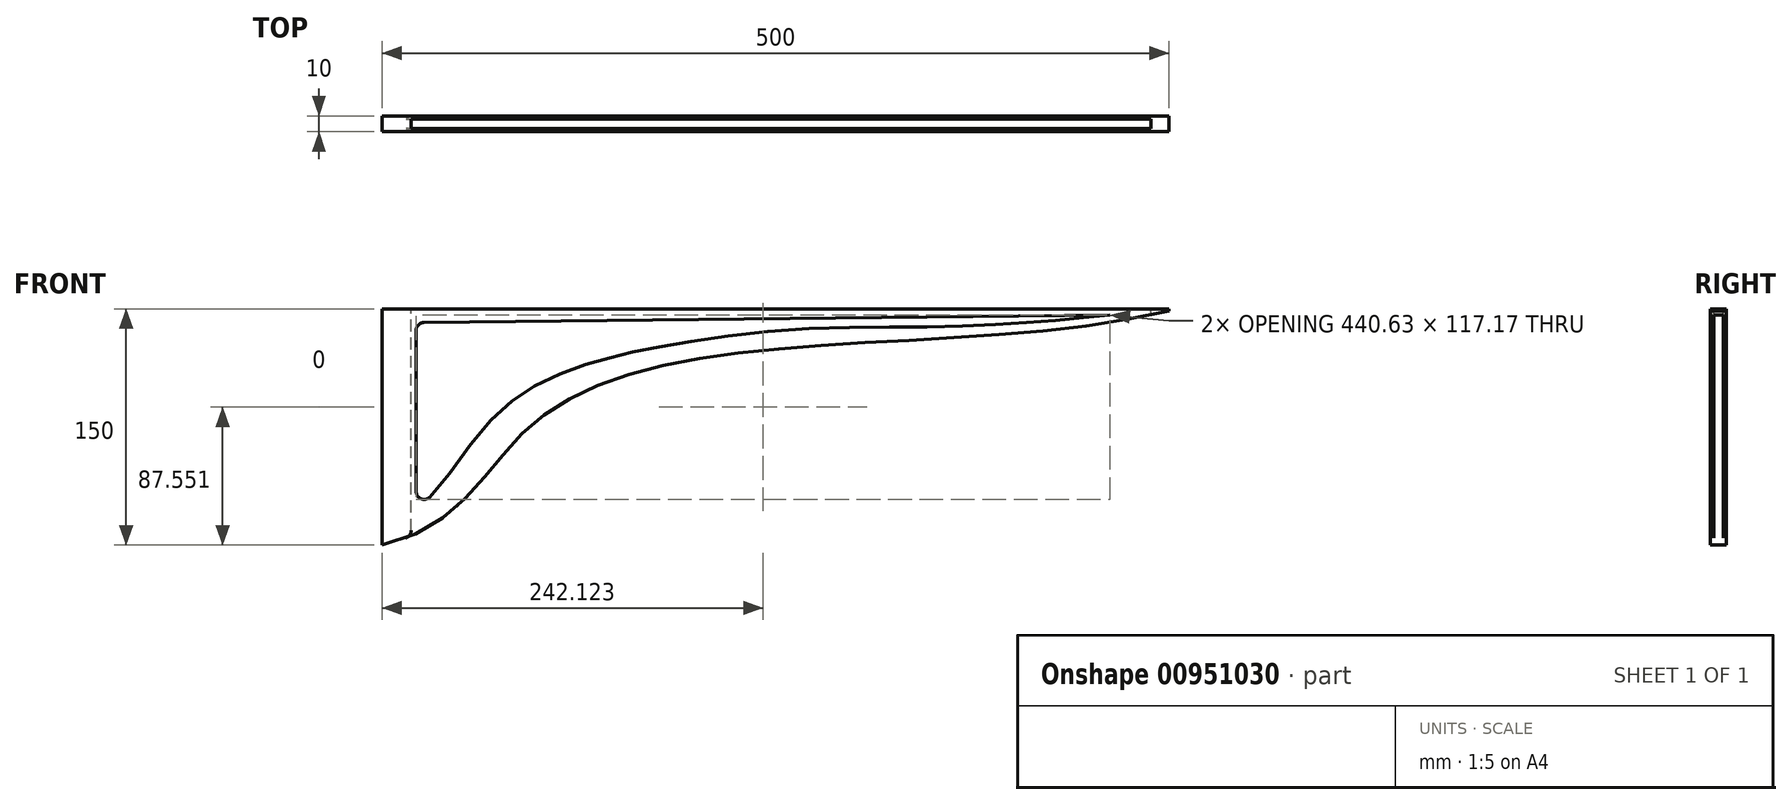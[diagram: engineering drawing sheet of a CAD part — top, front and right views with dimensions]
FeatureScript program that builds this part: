
annotation { "Feature Type Name" : "Feature", "Feature Type Description" : "" }
export const myFeature = defineFeature(function(context is Context, id is Id, definition is map)
    precondition{}
    {
        {
            var Q0;
            Q0=qCreatedBy(makeId("Front.planeOp"),FACE);
            var sketch = newSketch(context, id + "F0", { "sketchPlane" : qUnion([Q0])});
            skLineSegment(sketch, "E0.bottom", {"start": v(0, 0) * mm, "end": v(505, 0) * mm});
            skLineSegment(sketch, "E0.top", {"start": v(0, 10) * mm, "end": v(505, 10) * mm});
            skLineSegment(sketch, "E0.left", {"start": v(0, 0) * mm, "end": v(0, 10) * mm});
            skLineSegment(sketch, "E0.right", {"start": v(505, 0) * mm, "end": v(505, 10) * mm});
            skLineSegment(sketch, "E1.top", {"start": v(0, -150) * mm, "end": v(505, -150) * mm});
            skLineSegment(sketch, "E1.left", {"start": v(0, 0) * mm, "end": v(0, -150) * mm});
            skLineSegment(sketch, "E1.right", {"start": v(505, 0) * mm, "end": v(505, -150) * mm});
            skLineSegment(sketch, "E2.bottom", {"start": v(0, 0) * mm, "end": v(500, 0) * mm});
            skLineSegment(sketch, "E2.top", {"start": v(0, -150) * mm, "end": v(500, -150) * mm});
            skLineSegment(sketch, "E2.right", {"start": v(500, 0) * mm, "end": v(500, -150) * mm});
            skLineSegment(sketch, "E3", {"start": v(490, 0) * mm, "end": v(490, 10) * mm});
            skFitSpline(sketch, "E4", {"points": [v(505, 0) * mm, v(247.1, -25.85) * mm, v(94.95, -73.78) * mm, v(0, -150) * mm], "startDerivative": vector(-573.89, -147.3) * mm, "endDerivative": vector(-554.69, -117.76) * mm});
            skSolve(sketch);
        }
        {
            var Q0;
            {var subQ6=sQuery(id+"F0.wireOp",EDGE,"E1.left");Q0=makeQuery(id+"F0.imprint","IMPRINT",FACE,{"disambiguationData":[TD([[makeQuery(id+"F0.imprint","IMPRINT",EDGE,{"derivedFrom":subQ6}),1.0]])]});}
            extrude(context, id + "F1", {"entities" : qUnion([Q0]), "depth" : 10 * mm, "offsetDistance" : 25 * mm});
        }
        {
            var Q0;
            Q0=makeQuery(id+"F1.opExtrude","SWEPT_FACE",FACE,{"disambiguationData":[OSD([sQuery(id+"F0.wireOp",EDGE,"E0.bottom")])]});
            var sketch = newSketch(context, id + "F2", { "sketchPlane" : qUnion([Q0])});
            skLineSegment(sketch, "E5.bottom", {"start": v(18.59, -2) * mm, "end": v(488.37, -2) * mm});
            skLineSegment(sketch, "E5.top", {"start": v(18.59, -8) * mm, "end": v(488.37, -8) * mm});
            skLineSegment(sketch, "E5.left", {"start": v(18.59, -2) * mm, "end": v(18.59, -8) * mm});
            skLineSegment(sketch, "E5.right", {"start": v(488.37, -2) * mm, "end": v(488.37, -8) * mm});
            skLineSegment(sketch, "E6.bottom", {"start": v(500, 0) * mm, "end": v(490, 0) * mm});
            skLineSegment(sketch, "E6.top", {"start": v(500, -10) * mm, "end": v(490, -10) * mm});
            skLineSegment(sketch, "E6.left", {"start": v(500, 0) * mm, "end": v(500, -10) * mm});
            skLineSegment(sketch, "E6.right", {"start": v(490, 0) * mm, "end": v(490, -10) * mm});
            skSolve(sketch);
        }
        {
            var Q0;
            Q0=makeQuery(id+"F2.imprint","IMPRINT",FACE,{"disambiguationData":[TD([[makeQuery(id+"F2.imprint","IMPRINT",EDGE,{"derivedFrom":sQuery(id+"F2.wireOp",EDGE,"E5.bottom")}),-1.0]])]});
            extrude(context, id + "F3", {"entities" : qUnion([Q0]), "operationType" : NewBodyOperationType.REMOVE, "endBound" : BoundingType.THROUGH_ALL, "oppositeDirection" : true, "depth" : 25 * mm, "offsetDistance" : 25 * mm});
        }
        {
            var Q0;
            Q0=makeQuery(id+"F1.opExtrude","CAP_FACE",FACE,{"disambiguationData":[OSD([sQuery(id+"F0.wireOp",EDGE,"E0.bottom"),sQuery(id+"F0.wireOp",EDGE,"E1.left"),sQuery(id+"F0.wireOp",EDGE,"E2.right"),sQuery(id+"F0.wireOp",EDGE,"E4")])],"isStart":false});
            var sketch = newSketch(context, id + "F4", { "sketchPlane" : qUnion([Q0])});
            skLineSegment(sketch, "E7", {"start": v(21.8, -8.72) * mm, "end": v(21.8, -125.5) * mm});
            skFitSpline(sketch, "E8", {"points": [v(21.8, -125.5) * mm, v(58.58, -83.44) * mm, v(95.9, -49.58) * mm, v(137.81, -33) * mm, v(174.04, -24.63) * mm, v(256.72, -13.44) * mm, v(351.59, -11.36) * mm, v(415.67, -8.35) * mm, v(462.44, -3.86) * mm], "startDerivative": vector(255.35, 84.21) * mm, "endDerivative": vector(390.38, 41.35) * mm});
            skLineSegment(sketch, "E9", {"start": v(462.44, -3.86) * mm, "end": v(21.8, -8.72) * mm});
            skSolve(sketch);
        }
        {
            var Q0;
            Q0=makeQuery(id+"F4.imprint","IMPRINT",FACE,{"disambiguationData":[TD([[makeQuery(id+"F4.imprint","IMPRINT",EDGE,{"derivedFrom":sQuery(id+"F4.wireOp",EDGE,"E7")}),1.0]])]});
            extrude(context, id + "F5", {"entities" : qUnion([Q0]), "operationType" : NewBodyOperationType.REMOVE, "endBound" : BoundingType.THROUGH_ALL, "oppositeDirection" : true, "depth" : 25 * mm, "offsetDistance" : 25 * mm});
        }
        {
            var Q0;
            {var subQ0=sQuery(id+"F4.wireOp",EDGE,"E7");var subQ1=sQuery(id+"F4.wireOp",EDGE,"E8");Q0=makeQuery(id+"F5.boolean.opBoolean","COPY",EDGE,{"disambiguationData":[TD([makeQuery(id+"F3.boolean.opBoolean","COPY",FACE,{"derivedFrom":makeQuery(id+"F3.opExtrude","SWEPT_FACE",FACE,{"disambiguationData":[OSD([sQuery(id+"F2.wireOp",EDGE,"E5.top")])]})})])],"derivedFrom":makeQuery(id+"F5.opExtrude","SWEPT_EDGE",EDGE,{"disambiguationData":[OSD([subQ0,subQ1])]})});}
            var Q1;
            {var subQ0=sQuery(id+"F4.wireOp",EDGE,"E7");var subQ1=sQuery(id+"F4.wireOp",EDGE,"E8");Q1=makeQuery(id+"F5.boolean.opBoolean","COPY",EDGE,{"disambiguationData":[TD([makeQuery(id+"F3.boolean.opBoolean","COPY",FACE,{"derivedFrom":makeQuery(id+"F3.opExtrude","SWEPT_FACE",FACE,{"disambiguationData":[OSD([sQuery(id+"F2.wireOp",EDGE,"E5.bottom")])]})})])],"derivedFrom":makeQuery(id+"F5.opExtrude","SWEPT_EDGE",EDGE,{"disambiguationData":[OSD([subQ0,subQ1])]})});}
            fillet(context, id + "F6", {"entities" : qUnion([Q0, Q1]), "radius" : 5 * mm, "tangentPropagation" : true, "allowEdgeOverflow" : false});
        }
        {
            var Q0;
            {var subQ0=sQuery(id+"F4.wireOp",EDGE,"E7");var subQ1=sQuery(id+"F4.wireOp",EDGE,"E9");Q0=makeQuery(id+"F5.boolean.opBoolean","COPY",EDGE,{"disambiguationData":[TD([makeQuery(id+"F3.boolean.opBoolean","COPY",FACE,{"derivedFrom":makeQuery(id+"F3.opExtrude","SWEPT_FACE",FACE,{"disambiguationData":[OSD([sQuery(id+"F2.wireOp",EDGE,"E5.top")])]})})])],"derivedFrom":makeQuery(id+"F5.opExtrude","SWEPT_EDGE",EDGE,{"disambiguationData":[OSD([subQ0,subQ1])]})});}
            var Q1;
            {var subQ0=sQuery(id+"F4.wireOp",EDGE,"E9");var subQ1=sQuery(id+"F4.wireOp",EDGE,"E7");Q1=makeQuery(id+"F5.boolean.opBoolean","COPY",EDGE,{"disambiguationData":[TD([makeQuery(id+"F3.boolean.opBoolean","COPY",FACE,{"derivedFrom":makeQuery(id+"F3.opExtrude","SWEPT_FACE",FACE,{"disambiguationData":[OSD([sQuery(id+"F2.wireOp",EDGE,"E5.bottom")])]})})])],"derivedFrom":makeQuery(id+"F5.opExtrude","SWEPT_EDGE",EDGE,{"disambiguationData":[OSD([subQ1,subQ0])]})});}
            fillet(context, id + "F7", {"entities" : qUnion([Q0, Q1]), "radius" : 5 * mm, "tangentPropagation" : true, "allowEdgeOverflow" : false});
        }
        {
            var Q0;
            Q0=makeQuery(id+"F3.boolean.opBoolean","INTERSECT",EDGE,{"derivedFrom":[makeQuery(id+"F1.opExtrude","SWEPT_FACE",FACE,{"disambiguationData":[OSD([sQuery(id+"F0.wireOp",EDGE,"E4")])]}),makeQuery(id+"F3.opExtrude","SWEPT_FACE",FACE,{"disambiguationData":[OSD([sQuery(id+"F2.wireOp",EDGE,"E5.left")])]})]});
            var Q1;
            Q1=makeQuery(id+"F3.boolean.opBoolean","COPY",EDGE,{"derivedFrom":makeQuery(id+"F3.opExtrude","CAP_EDGE",EDGE,{"disambiguationData":[OSD([sQuery(id+"F2.wireOp",EDGE,"E5.left")])],"isStart":true})});
            fillet(context, id + "F8", {"entities" : qUnion([Q0, Q1]), "radius" : 5 * mm, "tangentPropagation" : true, "allowEdgeOverflow" : false});
        }
    });
